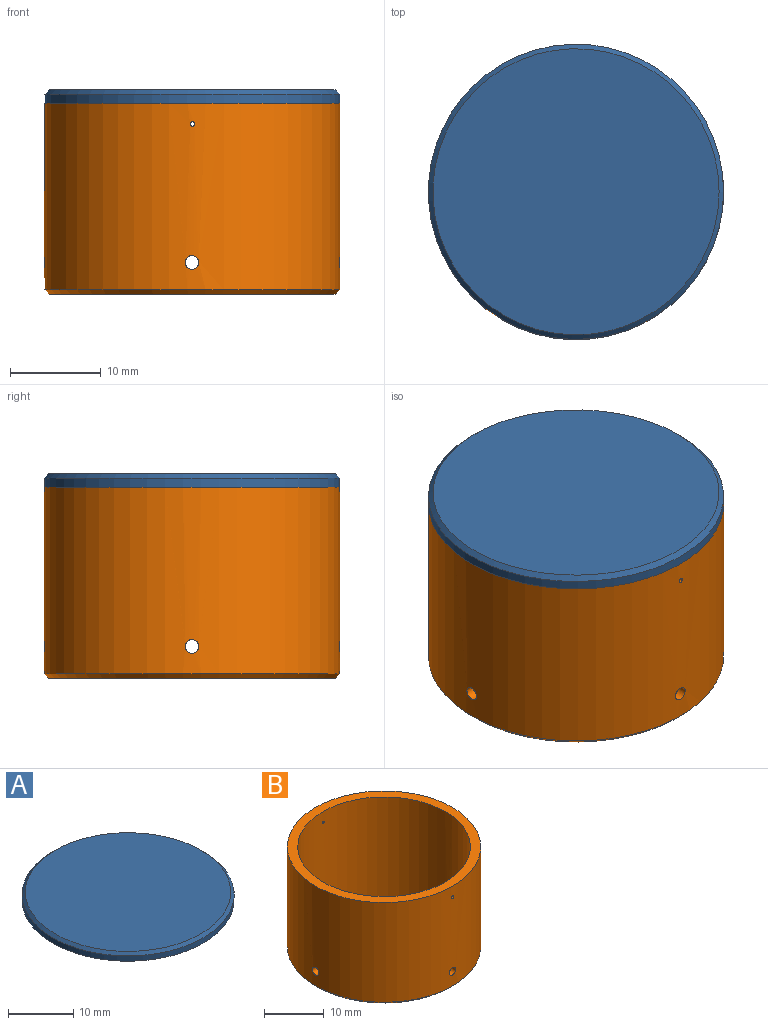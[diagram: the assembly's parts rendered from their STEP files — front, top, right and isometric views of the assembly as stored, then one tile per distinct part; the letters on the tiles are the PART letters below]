
ASSEMBLY  parts=2 mates=1
PART A: 4 faces, bbox 32.5x32.5x1.5 mm
  f0: cylinder r=16.25mm len=32.5mm, axis (0,0,-1), area 102.1mm2, adj f2,f3
  f1: plane 31.5x31.5mm, normal (0,0,1), area 779.3mm2, adj f3
  f2: plane 32.5x32.5mm, normal (0,0,-1), area 829.6mm2, adj f0
  f3: cone r=15.75mm half-angle=45deg, axis (0,0,-1), area 71.1mm2, adj f0,f1
PART B: 12 faces, bbox 32.5x32.5x21 mm
  f0: cylinder r=14.5mm len=29mm, axis (0,0,-1), area 1858.4mm2, adj f2,f4,f6,f7,f8,f9,f10,f11
  f1: cylinder r=16.25mm len=32.5mm, axis (0,0,-1), area -2095.2mm2, adj f2,f5,f6,f7,f8,f9,f10,f11
  f2: plane 32.5x32.5mm, normal (0,0,1), area 169.1mm2, adj f0,f1
  f3: plane 31.5x31.5mm, normal (0,0,-1), area 72.5mm2, adj f4,f5
  f4: cone r=15mm half-angle=45deg, axis (0,0,-1), area 65.5mm2, adj f0,f3
  f5: cone r=16.25mm half-angle=45deg, axis (0,0,1), area 71.1mm2, adj f1,f3
  f6: cylinder r=0.75mm len=1.77mm, axis (1,0,0), area 16.5mm2, adj f0,f1
  f7: cylinder r=0.75mm len=1.77mm, axis (1,0,0), area 8.3mm2, adj f0,f1
  f8: cylinder r=0.75mm len=1.77mm, axis (0,-1,0), area 8.3mm2, adj f0,f1
  f9: cylinder r=0.75mm len=1.77mm, axis (0,-1,0), area 8.3mm2, adj f0,f1
  f10: cylinder r=0.25mm len=1.75mm, axis (0,-1,0), area 2.7mm2, adj f0,f1
  f11: cylinder r=0.25mm len=1.75mm, axis (0,-1,0), area 2.7mm2, adj f0,f1
PLACE A rot(axis=(0,1,0),0deg) t=(-54.87,110.63,-5.44)mm
PLACE B rot(axis=(0,1,0),0deg) t=(-54.87,110.63,-26.44)mm
MATE fastened B.f0 <-> A.f0  axis (0,0,1) through (-54.87,110.63,-5.44)mm
